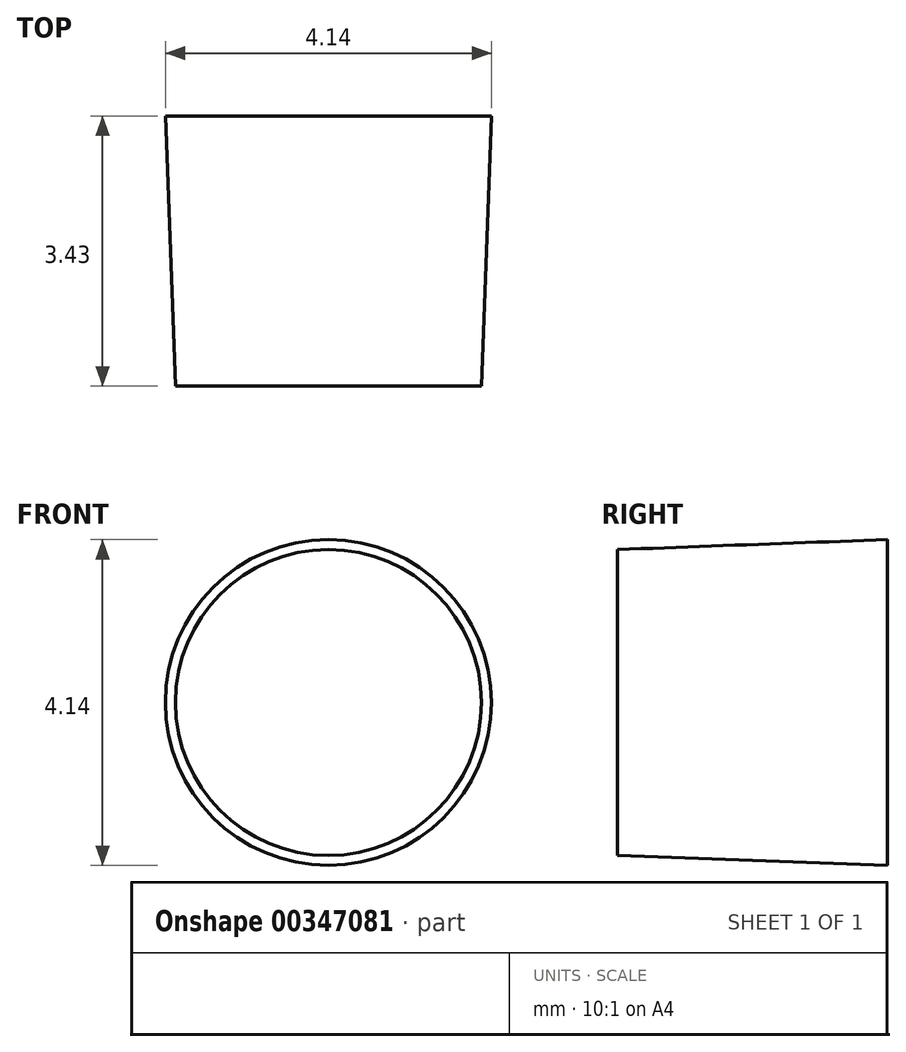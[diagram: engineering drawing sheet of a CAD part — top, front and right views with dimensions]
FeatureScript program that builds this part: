
annotation { "Feature Type Name" : "Feature", "Feature Type Description" : "" }
export const myFeature = defineFeature(function(context is Context, id is Id, definition is map)
    precondition{}
    {
        {
            var Q0;
            Q0=qCreatedBy(makeId("Top.planeOp"),FACE);
            var sketch = newSketch(context, id + "F0", { "sketchPlane" : qUnion([Q0])});
            skLineSegment(sketch, "E0", {"start": v(-12.81, 0) * mm, "end": v(-10.74, 0) * mm});
            skLineSegment(sketch, "E1", {"start": v(-12.68, -3.43) * mm, "end": v(-10.74, -3.43) * mm});
            skPoint(sketch, "E2", {"position": v(-10.74, 0) * mm});
            skPoint(sketch, "E3", {"position": v(-10.74, -3.43) * mm});
            skLineSegment(sketch, "E4", {"start": v(-12.81, 0) * mm, "end": v(-12.68, -3.43) * mm});
            skLineSegment(sketch, "E5", {"start": v(-8.67, 0) * mm, "end": v(-8.8, -3.43) * mm, "construction": true});
            skLineSegment(sketch, "E6", {"start": v(-10.74, 0) * mm, "end": v(-10.74, -3.43) * mm});
            skLineSegment(sketch, "E7", {"start": v(-10.74, 0) * mm, "end": v(-8.67, 0) * mm, "construction": true});
            skLineSegment(sketch, "E8", {"start": v(-10.74, -3.43) * mm, "end": v(-8.8, -3.43) * mm, "construction": true});
            skSolve(sketch);
        }
        {
            var Q0;
            Q0 = qSketchRegion(id + "F0", true);
            var Q1;
            Q1=sQuery(id+"F0.wireOp",EDGE,"E6");
            revolve(context, id + "F1", {"surfaceOperationType" : NewSurfaceOperationType.NEW, "entities" : qUnion([Q0]), "axis" : qUnion([Q1]), "revolveType" : RevolveType.FULL});
        }
    });
